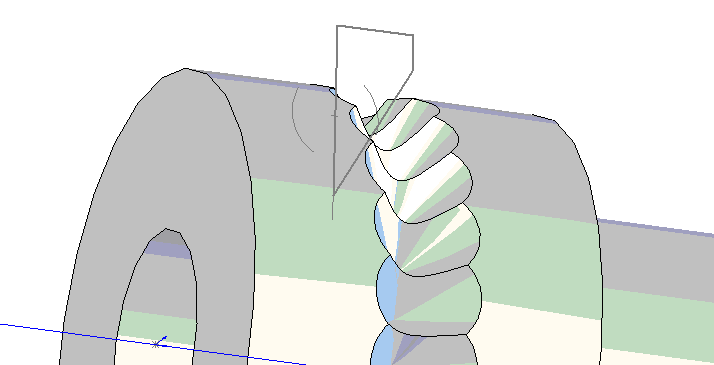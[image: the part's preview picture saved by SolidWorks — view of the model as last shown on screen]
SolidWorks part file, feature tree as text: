
SOLIDWORKS PART (.sldprt)
format: sldprt  version: not decoded by parser v0  size: 259,584 bytes
history: native  units: mm
features: sketch x2, revolve x1, cut_revolve x1, pattern_circular x1 (+11 scaffold rows collapsed)
feature tree (16):
  scaffold x11  (default folders/planes/origin — collapsed)
  sketch  "Sketch1"  dims[D1=2.0066mm D2=3.175mm D3=6.35mm D4=6.35mm D5=4.7625mm]
  revolve  "Revolve1"  Angle=360deg
  sketch  "Sketch3"  dims[c1.D2=1.5875mm c1.D6=1.5875mm c1.D1=3.175mm c1.D3=2.7686mm c1.D4=1.5875mm c1.D5=~0.939273mm c2.D5=~122.32075deg c3.D5=~2.08969mm c4.D5=30.0deg c4.D4=1.0668mm c4.D6=0.7112mm c5.D4=0.254mm]
  cut_revolve  "Cut-Revolve2"  Angle=360deg
  pattern_circular  "CirPattern1"  Count=24 Angle=15deg
decode coverage: 5 of 5 modeling features carry decoded parameters
note: ~ marks probable driven/reference dimensions
note: suppression state not decoded; provenance and decode notes live in map.json
